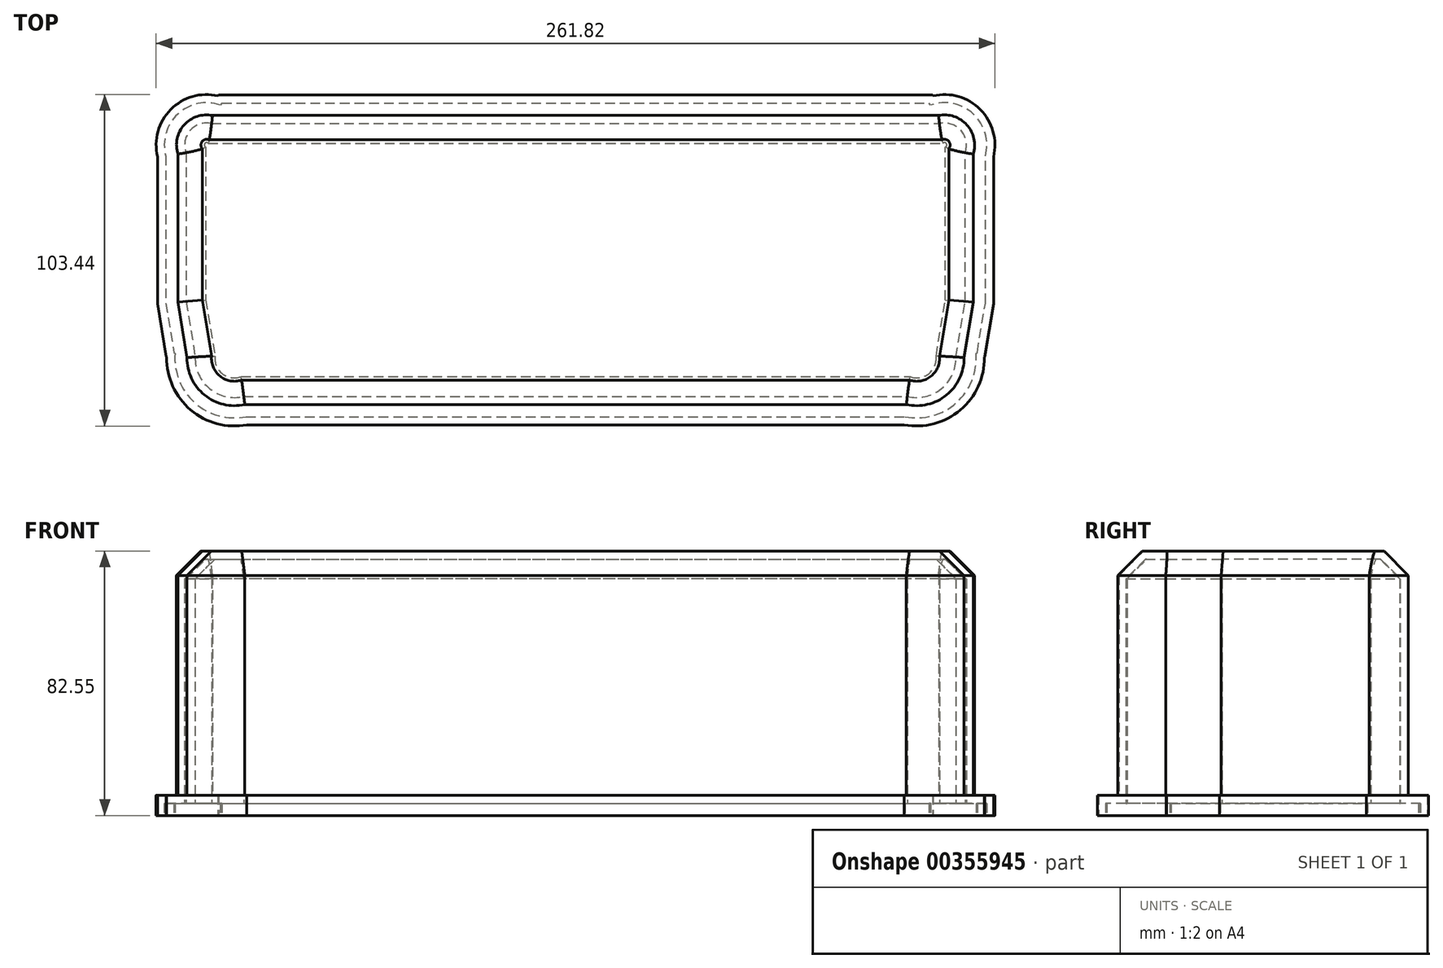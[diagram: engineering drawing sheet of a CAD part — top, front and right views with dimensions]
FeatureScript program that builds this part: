
annotation { "Feature Type Name" : "Feature", "Feature Type Description" : "" }
export const myFeature = defineFeature(function(context is Context, id is Id, definition is map)
    precondition{}
    {
        {
            var Q0;
            Q0=qCreatedBy(makeId("Top.planeOp"),FACE);
            var sketch = newSketch(context, id + "F0", { "sketchPlane" : qUnion([Q0])});
            skLineSegment(sketch, "E0", {"start": v(-17, -101.28) * mm, "end": v(205.83, -101.28) * mm});
            skLineSegment(sketch, "E1", {"start": v(-17, -101.28) * mm, "end": v(-17.23, -101.5) * mm});
            skLineSegment(sketch, "E2", {"start": v(-36.06, -120.33) * mm, "end": v(-36.06, -166.4) * mm});
            skLineSegment(sketch, "E3", {"start": v(-36.06, -166.4) * mm, "end": v(-33.34, -182.92) * mm});
            skLineSegment(sketch, "E4", {"start": v(-33.34, -182.92) * mm, "end": v(-33.2, -183.03) * mm});
            skLineSegment(sketch, "E5", {"start": v(-8.27, -204.19) * mm, "end": v(197.1, -204.19) * mm});
            skLineSegment(sketch, "E6", {"start": v(222.03, -183.03) * mm, "end": v(222.16, -182.92) * mm});
            skLineSegment(sketch, "E7", {"start": v(222.16, -182.92) * mm, "end": v(224.88, -166.4) * mm});
            skLineSegment(sketch, "E8", {"start": v(224.88, -166.4) * mm, "end": v(224.88, -120.33) * mm});
            skLineSegment(sketch, "E9", {"start": v(206.05, -101.5) * mm, "end": v(205.83, -101.28) * mm});
            skArc(sketch, "E10", {"start": v(-33.2, -183.03) * mm, "mid": v(-25.73, -199.54) * mm, "end": v(-8.22, -204.19) * mm});
            skArc(sketch, "E11", {"start": v(-17.23, -101.5) * mm, "mid": v(-31.95, -105.77) * mm, "end": v(-36.06, -120.53) * mm});
            skArc(sketch, "E12.MirrorC", {"start": v(206.05, -101.5) * mm, "mid": v(220.77, -105.77) * mm, "end": v(224.88, -120.53) * mm});
            skArc(sketch, "E13.MirrorC", {"start": v(222.03, -183.03) * mm, "mid": v(214.55, -199.54) * mm, "end": v(197.04, -204.19) * mm});
            skPoint(sketch, "E14.start.orphan", {"position": v(94.41, -101.28) * mm});
            skSolve(sketch);
        }
        {
            var Q0;
            Q0=qSketchRegion(id+"F0",true);
            extrude(context, id + "F1", {"entities" : qUnion([Q0]), "depth" : 6.35 * mm});
        }
        {
            var Q0;
            Q0=makeQuery(id+"F1.opExtrude","CAP_FACE",FACE,{"disambiguationData":[OSD([sQuery(id+"F0.wireOp",EDGE,"E0"),sQuery(id+"F0.wireOp",EDGE,"E1"),sQuery(id+"F0.wireOp",EDGE,"E2"),sQuery(id+"F0.wireOp",EDGE,"E3"),sQuery(id+"F0.wireOp",EDGE,"E4"),sQuery(id+"F0.wireOp",EDGE,"E5"),sQuery(id+"F0.wireOp",EDGE,"E6"),sQuery(id+"F0.wireOp",EDGE,"E7"),sQuery(id+"F0.wireOp",EDGE,"E8"),sQuery(id+"F0.wireOp",EDGE,"E9"),sQuery(id+"F0.wireOp",EDGE,"E10"),sQuery(id+"F0.wireOp",EDGE,"E11"),sQuery(id+"F0.wireOp",EDGE,"E12.MirrorC"),sQuery(id+"F0.wireOp",EDGE,"E13.MirrorC")])],"isStart":false});
            var sketch = newSketch(context, id + "F2", { "sketchPlane" : qUnion([Q0])});
            skLineSegment(sketch, "E15.0", {"start": v(-18.91, -107.63) * mm, "end": v(207.74, -107.63) * mm});
            skArc(sketch, "E16.0", {"start": v(-18.91, -107.63) * mm, "mid": v(-27.75, -110.57) * mm, "end": v(-29.7, -119.68) * mm});
            skLineSegment(sketch, "E17.0", {"start": v(-29.7, -165.88) * mm, "end": v(-26.86, -183.2) * mm});
            skLineSegment(sketch, "E17.1", {"start": v(-29.7, -119.68) * mm, "end": v(-29.7, -165.88) * mm});
            skArc(sketch, "E18.0", {"start": v(-26.86, -183.2) * mm, "mid": v(-21.4, -194.88) * mm, "end": v(-8.85, -197.84) * mm});
            skLineSegment(sketch, "E19.0", {"start": v(-8.85, -197.84) * mm, "end": v(197.67, -197.84) * mm});
            skArc(sketch, "E20.0", {"start": v(215.68, -183.2) * mm, "mid": v(210.22, -194.88) * mm, "end": v(197.67, -197.84) * mm});
            skArc(sketch, "E21.0", {"start": v(207.74, -107.63) * mm, "mid": v(216.58, -110.57) * mm, "end": v(218.53, -119.68) * mm});
            skLineSegment(sketch, "E21.1", {"start": v(218.53, -165.88) * mm, "end": v(218.53, -119.68) * mm});
            skLineSegment(sketch, "E21.2", {"start": v(215.68, -183.2) * mm, "end": v(218.53, -165.88) * mm});
            skSolve(sketch);
        }
        {
            var Q0;
            Q0=makeQuery(id+"F2.imprint","IMPRINT",FACE,{"disambiguationData":[TD([[makeQuery(id+"F2.imprint","IMPRINT",EDGE,{"derivedFrom":sQuery(id+"F2.wireOp",EDGE,"E15.0")}),-1.0]])]});
            extrude(context, id + "F3", {"entities" : qUnion([Q0]), "operationType" : NewBodyOperationType.ADD, "depth" : 76.2 * mm});
        }
        {
            var Q0;
            Q0=makeQuery(id+"F3.opExtrude","CAP_FACE",FACE,{"disambiguationData":[OSD([sQuery(id+"F2.wireOp",EDGE,"E15.0"),sQuery(id+"F2.wireOp",EDGE,"E16.0"),sQuery(id+"F2.wireOp",EDGE,"E17.0"),sQuery(id+"F2.wireOp",EDGE,"E17.1"),sQuery(id+"F2.wireOp",EDGE,"E18.0"),sQuery(id+"F2.wireOp",EDGE,"E19.0"),sQuery(id+"F2.wireOp",EDGE,"E20.0"),sQuery(id+"F2.wireOp",EDGE,"E21.0"),sQuery(id+"F2.wireOp",EDGE,"E21.1"),sQuery(id+"F2.wireOp",EDGE,"E21.2")])],"isStart":false});
            chamfer(context, id + "F4", {"entities" : qUnion([Q0]), "width" : 7.62 * mm, "tangentPropagation" : true});
        }
        {
            var Q0;
            Q0=makeQuery(id+"F1.opExtrude","CAP_FACE",FACE,{"disambiguationData":[OSD([sQuery(id+"F0.wireOp",EDGE,"E0"),sQuery(id+"F0.wireOp",EDGE,"E1"),sQuery(id+"F0.wireOp",EDGE,"E2"),sQuery(id+"F0.wireOp",EDGE,"E3"),sQuery(id+"F0.wireOp",EDGE,"E4"),sQuery(id+"F0.wireOp",EDGE,"E5"),sQuery(id+"F0.wireOp",EDGE,"E6"),sQuery(id+"F0.wireOp",EDGE,"E7"),sQuery(id+"F0.wireOp",EDGE,"E8"),sQuery(id+"F0.wireOp",EDGE,"E9"),sQuery(id+"F0.wireOp",EDGE,"E10"),sQuery(id+"F0.wireOp",EDGE,"E11"),sQuery(id+"F0.wireOp",EDGE,"E12.MirrorC"),sQuery(id+"F0.wireOp",EDGE,"E13.MirrorC")])],"isStart":true});
            shell(context, id + "F5", {"entities" : qUnion([Q0]), "thickness" : 2.54 * mm});
        }
    });
